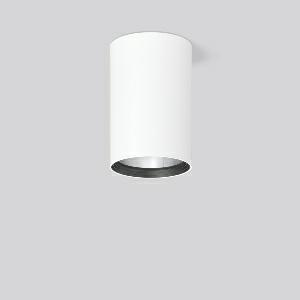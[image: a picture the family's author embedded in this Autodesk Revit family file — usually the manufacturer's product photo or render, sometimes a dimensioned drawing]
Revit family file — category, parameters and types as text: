
# Revit family: heledon_maxi_a_931217_002_2_657b
name_source: partatom
category: Lighting Fixtures
units: mm (PartAtom-declared; Revit-internal decimal feet)

## family parameters
Cut with Voids When Loaded = No
Host = Face
Light Source = No
Part Type = Normal
Room Calculation Point = No
Round Connector Dimension = Use Diameter
Shared = No

## types (1)
- HELEDON maxi A (1 x LED Modul 927, 3150 lm, 2700)
    Apparent Load = 25 VA
    Approval mark = CE
    CIE Flux Codes = 100 100 100 100 100
    Color Rendering = 92
    Color Temperature = 2700
    Default Elevation = 1800 mm
    Description = Series: HELEDON maxi
Cylindrical surface-mounted downlight. Housing: die-cast aluminium, powder-coated. Internal ceiling frame polycarbonate with bayonet mounting. Black plastic ring and recessed LED to prevent glare from the side. Optical assembly with reflector made of MIRO-Silver with 98% total light reflection for outstanding efficiency - can be changed without tools. Best colour rendering index Ra>90. Suitable for Ceiling mounting. Easy installation with a separate ceiling frame with bayonet mounting and plug connection. Driver integrated. Connected via plug-in connector. High quality converter without flickering and stroboscopic effect. The following accessories can be mounted without use of tools: interchangeable lenses, decorative glasses, honeycomb louvre, clear and frosted diffusers, white interchangeable plastic ring. 
Colour: traffic white, matt (RAL 9016)
Diameter: 123 mm
Height: 183 mm
Lamp: LED
Socket: without socket
Colour temperature: 2700K
Colour rendering index (CRI): 92
System power: 25 W
Rated luminous flux: 3150 lm
Luminous efficiency: 126 lm/W
Control gear: Regulated power supply
Protection class: I
Type of protection: IP 20
    Height = 183 mm
    Lamp = 1 x LED Modul 927
    Lamp Light Flux = 3150 lm
    Lamp count = 1
    Length = 123 mm
    Lifetime = 50000 h
    Luminous efficacy = 126 lm/W
    Manufacturer = RZB
    ModVariant = No
    Model = 931217.002.2
    Mounting Place = Ceiling
    Mounting Type = Surface mounted
    Number of Poles = 1
    OnlyDefault = Yes
    Power Factor = 1
    Product Name = HELEDON maxi A
    Product group = Surface mounted downlights
    ProductGroupID = 302
    Protection Class = Protection class I
    Protection Degree = IP 20
    RLX_Detail_Level = 1
    RLX_Emergency_Light_Flux = 0 lm
    RLX_Emergency_Type = 0
    RLX_Emergency_Type_DB = No
    RlxData = <blob elided: 97777 chars, md5=b4487884>
    Socket = socket
    Standby Power = 0 W
    System Light Flux = 3150 lm
    System Power = 25 W
    Type Comments = Product without accessories
    Type Image = 931192.002.jpg
    URL = http://relux.com
    VarID = ---
    Voltage = 230 V
    Voltage Range = 220-240 V
    Weight = 0.00 kg
    Width = 0 mm  [stored 0 ft]

note: [stored X ft] marks values corroborated as IEEE doubles in the binary element streams (Revit-internal decimal feet)

## geometry (parser evidence)
native form markers: Blend x4, Sweep x12
no freeform markers — native parametric forms only
